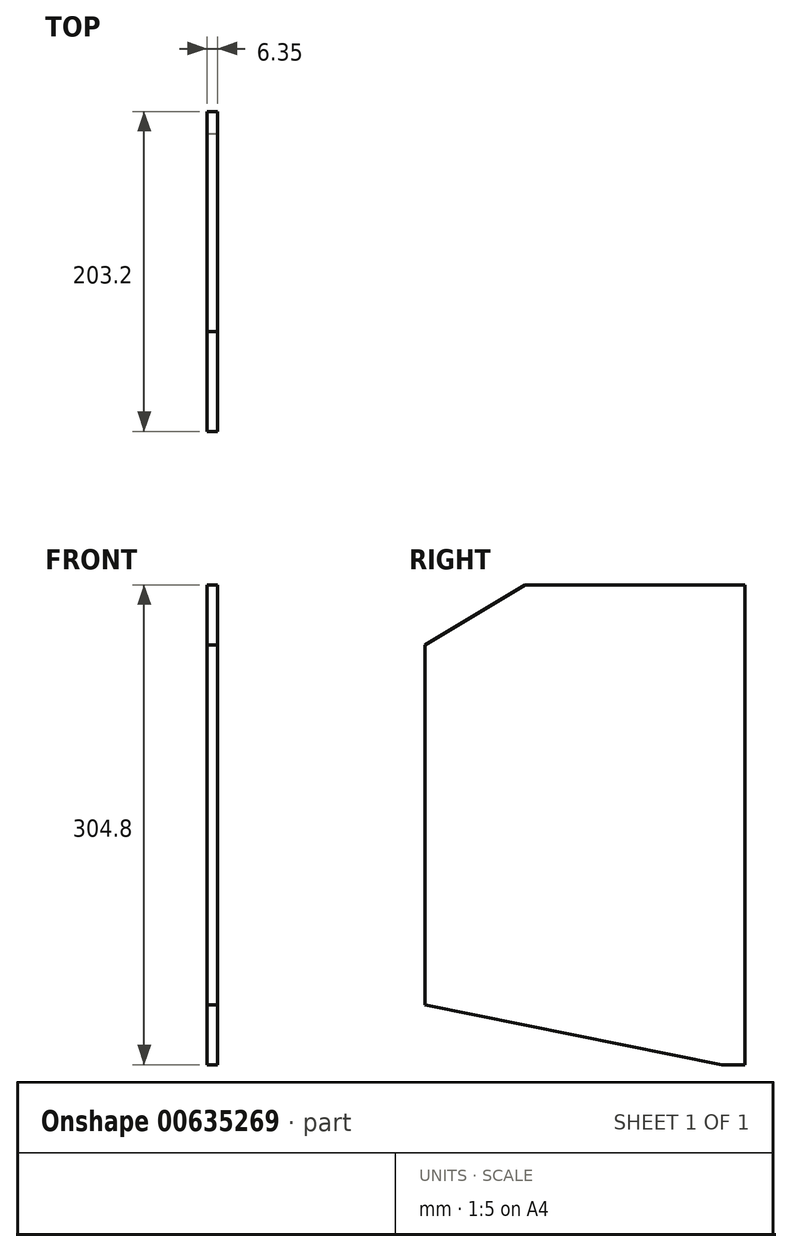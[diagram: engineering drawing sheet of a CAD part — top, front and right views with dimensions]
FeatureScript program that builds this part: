
annotation { "Feature Type Name" : "Feature", "Feature Type Description" : "" }
export const myFeature = defineFeature(function(context is Context, id is Id, definition is map)
    precondition{}
    {
        {
            var Q0;
            Q0=qCreatedBy(makeId("Right.planeOp"),FACE);
            var sketch = newSketch(context, id + "F0", { "sketchPlane" : qUnion([Q0])});
            skLineSegment(sketch, "E0.bottom", {"start": v(101.6, 152.4) * mm, "end": v(-38.1, 152.4) * mm});
            skLineSegment(sketch, "E0.top", {"start": v(101.6, -152.4) * mm, "end": v(-38.1, -152.4) * mm});
            skLineSegment(sketch, "E0.left", {"start": v(101.6, 152.4) * mm, "end": v(101.6, -152.4) * mm});
            skLineSegment(sketch, "E0.right", {"start": v(-101.6, 152.4) * mm, "end": v(-101.6, -152.4) * mm});
            skPoint(sketch, "E0.middle", {"position": v(0, 0) * mm});
            skLineSegment(sketch, "E1", {"start": v(-101.6, 114.3) * mm, "end": v(-38.1, 152.4) * mm});
            skLineSegment(sketch, "E2", {"start": v(-101.6, -114.3) * mm, "end": v(-38.1, -152.4) * mm});
            skSolve(sketch);
        }
        {
            var Q0;
            Q0 = qSketchRegion(id + "F0", true);
            extrude(context, id + "F1", {"entities" : qUnion([Q0]), "depth" : 6.35 * mm, "offsetDistance" : 25.4 * mm});
        }
        {
            var Q0;
            Q0=makeQuery(id+"F1.opExtrude","CAP_FACE",FACE,{"disambiguationData":[OSD([sQuery(id+"F0.wireOp",EDGE,"E0.bottom"),sQuery(id+"F0.wireOp",EDGE,"E0.top"),sQuery(id+"F0.wireOp",EDGE,"E0.left"),sQuery(id+"F0.wireOp",EDGE,"E0.right"),sQuery(id+"F0.wireOp",EDGE,"E1"),sQuery(id+"F0.wireOp",EDGE,"E2")])],"isStart":true});
            var sketch = newSketch(context, id + "F2", { "sketchPlane" : qUnion([Q0])});
            skLineSegment(sketch, "E3", {"start": v(101.6, -114.3) * mm, "end": v(-87.16, -152.4) * mm});
            skLineSegment(sketch, "E4", {"start": v(-87.16, -152.4) * mm, "end": v(38.1, -152.4) * mm});
            skLineSegment(sketch, "E5", {"start": v(38.1, -152.4) * mm, "end": v(101.6, -114.3) * mm});
            skSolve(sketch);
        }
        {
            var Q0;
            Q0 = qSketchRegion(id + "F2", true);
            extrude(context, id + "F3", {"entities" : qUnion([Q0]), "operationType" : NewBodyOperationType.REMOVE, "oppositeDirection" : true, "depth" : 25.4 * mm, "offsetDistance" : 25.4 * mm});
        }
    });
